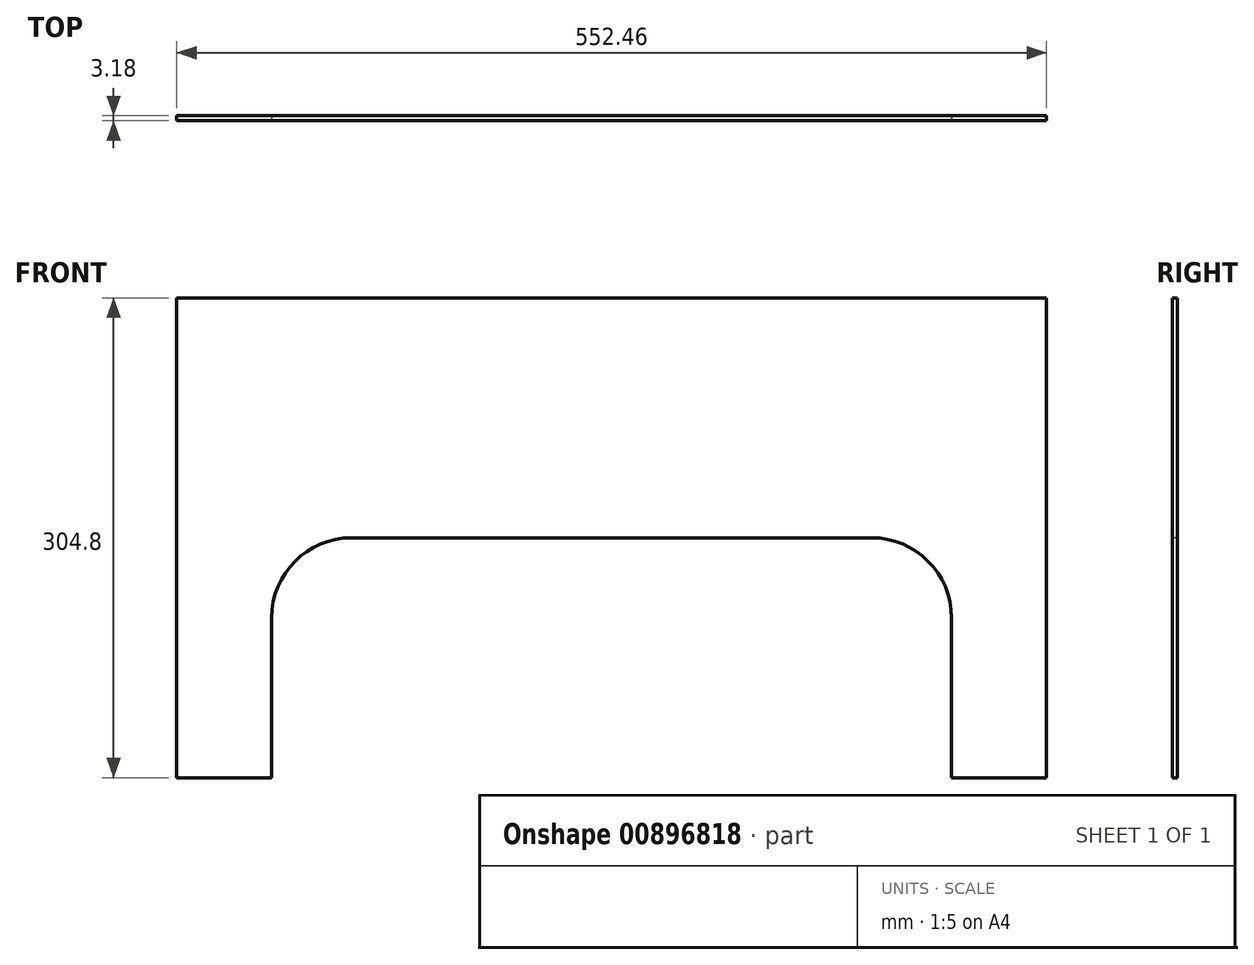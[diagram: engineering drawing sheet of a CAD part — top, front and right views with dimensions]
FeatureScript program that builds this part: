
annotation { "Feature Type Name" : "Feature", "Feature Type Description" : "" }
export const myFeature = defineFeature(function(context is Context, id is Id, definition is map)
    precondition{}
    {
        {
            var Q0;
            Q0=qCreatedBy(makeId("Front.planeOp"),FACE);
            var sketch = newSketch(context, id + "F0", { "sketchPlane" : qUnion([Q0])});
            skLineSegment(sketch, "E0.bottom", {"start": v(276.23, -152.4) * mm, "end": v(-276.23, -152.4) * mm});
            skLineSegment(sketch, "E0.top", {"start": v(276.23, 152.4) * mm, "end": v(-276.23, 152.4) * mm});
            skLineSegment(sketch, "E0.left", {"start": v(276.23, -152.4) * mm, "end": v(276.23, 152.4) * mm});
            skLineSegment(sketch, "E0.right", {"start": v(-276.23, -152.4) * mm, "end": v(-276.23, 152.4) * mm});
            skPoint(sketch, "E0.middle", {"position": v(0, 0) * mm});
            skSolve(sketch);
        }
        {
            var Q0;
            Q0=makeQuery(id+"F0.imprint","IMPRINT",FACE,{"disambiguationData":[TD([[makeQuery(id+"F0.imprint","IMPRINT",EDGE,{"derivedFrom":sQuery(id+"F0.wireOp",EDGE,"E0.bottom")}),-1.0]])]});
            extrude(context, id + "F1", {"entities" : qUnion([Q0]), "depth" : 3.17 * mm, "offsetDistance" : 25.4 * mm});
        }
        {
            var Q0;
            Q0=makeQuery(id+"F1.opExtrude","CAP_FACE",FACE,{"disambiguationData":[OSD([sQuery(id+"F0.wireOp",EDGE,"E0.bottom"),sQuery(id+"F0.wireOp",EDGE,"E0.top"),sQuery(id+"F0.wireOp",EDGE,"E0.left"),sQuery(id+"F0.wireOp",EDGE,"E0.right")])],"isStart":false});
            var sketch = newSketch(context, id + "F2", { "sketchPlane" : qUnion([Q0])});
            skLineSegment(sketch, "E1.0.0", {"start": v(276.23, -152.4) * mm, "end": v(276.23, 152.4) * mm, "construction": true});
            skLineSegment(sketch, "E1.0.1", {"start": v(276.23, 152.4) * mm, "end": v(-276.23, 152.4) * mm, "construction": true});
            skLineSegment(sketch, "E1.0.2", {"start": v(-276.23, 152.4) * mm, "end": v(-276.23, -152.4) * mm, "construction": true});
            skLineSegment(sketch, "E1.0.3", {"start": v(-276.23, -152.4) * mm, "end": v(276.23, -152.4) * mm, "construction": true});
            skLineSegment(sketch, "E2", {"start": v(0, 0) * mm, "end": v(0, -152.4) * mm, "construction": true});
            skLineSegment(sketch, "E3.bottom", {"start": v(-215.9, -152.4) * mm, "end": v(215.9, -152.4) * mm});
            skLineSegment(sketch, "E3.top", {"start": v(-215.9, 0) * mm, "end": v(215.9, 0) * mm});
            skLineSegment(sketch, "E3.left", {"start": v(-215.9, -152.4) * mm, "end": v(-215.9, 0) * mm});
            skLineSegment(sketch, "E3.right", {"start": v(215.9, -152.4) * mm, "end": v(215.9, 0) * mm});
            skSolve(sketch);
        }
        {
            var Q0;
            Q0 = qSketchRegion(id + "F2", true);
            extrude(context, id + "F3", {"entities" : qUnion([Q0]), "operationType" : NewBodyOperationType.REMOVE, "endBound" : BoundingType.THROUGH_ALL, "oppositeDirection" : true, "depth" : 25.4 * mm, "offsetDistance" : 25.4 * mm});
        }
        {
            var Q0;
            Q0=makeQuery(id+"F3.boolean.opBoolean","COPY",EDGE,{"derivedFrom":makeQuery(id+"F3.opExtrude","SWEPT_EDGE",EDGE,{"disambiguationData":[OSD([sQuery(id+"F2.wireOp",EDGE,"E3.top"),sQuery(id+"F2.wireOp",EDGE,"E3.left")])]})});
            var Q1;
            Q1=makeQuery(id+"F3.boolean.opBoolean","COPY",EDGE,{"derivedFrom":makeQuery(id+"F3.opExtrude","SWEPT_EDGE",EDGE,{"disambiguationData":[OSD([sQuery(id+"F2.wireOp",EDGE,"E3.top"),sQuery(id+"F2.wireOp",EDGE,"E3.right")])]})});
            fillet(context, id + "F4", {"entities" : qUnion([Q0, Q1]), "radius" : 50.8 * mm, "tangentPropagation" : true, "allowEdgeOverflow" : false});
        }
    });
